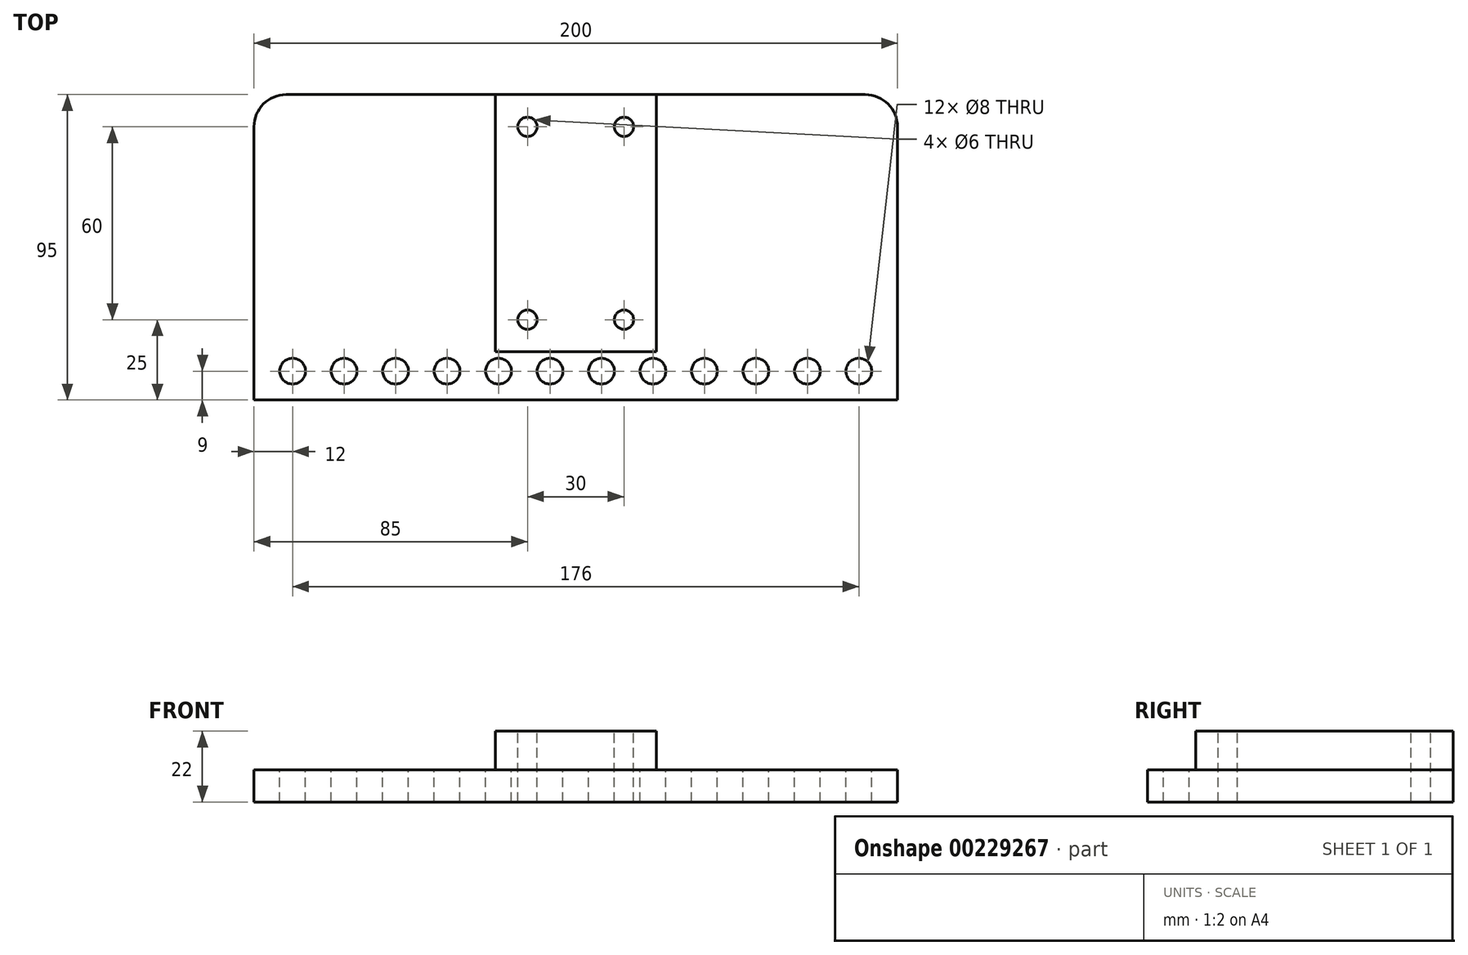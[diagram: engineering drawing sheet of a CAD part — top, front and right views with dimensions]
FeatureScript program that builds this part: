
annotation { "Feature Type Name" : "Feature", "Feature Type Description" : "" }
export const myFeature = defineFeature(function(context is Context, id is Id, definition is map)
    precondition{}
    {
        {
            var Q0;
            Q0=qCreatedBy(makeId("Top.planeOp"),FACE);
            var sketch = newSketch(context, id + "F0", { "sketchPlane" : qUnion([Q0])});
            skLineSegment(sketch, "E0.bottom", {"start": v(0, 0) * mm, "end": v(200, 0) * mm});
            skLineSegment(sketch, "E0.top", {"start": v(10, 95) * mm, "end": v(190, 95) * mm});
            skLineSegment(sketch, "E0.left", {"start": v(0, 0) * mm, "end": v(0, 85) * mm});
            skLineSegment(sketch, "E0.right", {"start": v(200, 0) * mm, "end": v(200, 85) * mm});
            skCircle(sketch, "E1", {"center": v(85, 85) * mm, "radius": 3 * mm});
            skCircle(sketch, "E2.0.1.0", {"center": v(85, 25) * mm, "radius": 3 * mm});
            skCircle(sketch, "E2.1.0.0", {"center": v(115, 85) * mm, "radius": 3 * mm});
            skCircle(sketch, "E2.1.1.0", {"center": v(115, 25) * mm, "radius": 3 * mm});
            skLineSegment(sketch, "E2.direction1", {"start": v(85, 85) * mm, "end": v(115, 85) * mm, "construction": true});
            skLineSegment(sketch, "E2.direction2", {"start": v(85, 85) * mm, "end": v(85, 25) * mm, "construction": true});
            skPoint(sketch, "E3.visualSharp", {"position": v(0, 95) * mm});
            skArc(sketch, "E3.filletArc", {"start": v(10, 95) * mm, "mid": v(2.93, 92.07) * mm, "end": v(0, 85) * mm});
            skPoint(sketch, "E4.visualSharp", {"position": v(200, 95) * mm});
            skArc(sketch, "E4.filletArc", {"start": v(200, 85) * mm, "mid": v(197.07, 92.07) * mm, "end": v(190, 95) * mm});
            skCircle(sketch, "E5", {"center": v(12, 9) * mm, "radius": 4 * mm});
            skCircle(sketch, "E6.1.0.0", {"center": v(28, 9) * mm, "radius": 4 * mm});
            skCircle(sketch, "E6.2.0.0", {"center": v(44, 9) * mm, "radius": 4 * mm});
            skCircle(sketch, "E6.3.0.0", {"center": v(60, 9) * mm, "radius": 4 * mm});
            skLineSegment(sketch, "E6.direction1", {"start": v(12, 9) * mm, "end": v(28, 9) * mm, "construction": true});
            skLineSegment(sketch, "E7", {"start": v(75, 95) * mm, "end": v(75, 15) * mm});
            skLineSegment(sketch, "E8", {"start": v(125, 95) * mm, "end": v(125, 15) * mm});
            skLineSegment(sketch, "E9", {"start": v(75, 15) * mm, "end": v(125, 15) * mm});
            skPoint(sketch, "E10.orphan", {"position": v(125, 0) * mm});
            skPoint(sketch, "E11.orphan", {"position": v(75, 0) * mm});
            skCircle(sketch, "E12.0.4.0", {"center": v(76, 9) * mm, "radius": 4 * mm});
            skCircle(sketch, "E12.0.5.0", {"center": v(92, 9) * mm, "radius": 4 * mm});
            skCircle(sketch, "E13.0.6.0", {"center": v(108, 9) * mm, "radius": 4 * mm});
            skCircle(sketch, "E13.0.7.0", {"center": v(124, 9) * mm, "radius": 4 * mm});
            skCircle(sketch, "E13.0.8.0", {"center": v(140, 9) * mm, "radius": 4 * mm});
            skCircle(sketch, "E14.0.9.0", {"center": v(156, 9) * mm, "radius": 4 * mm});
            skCircle(sketch, "E15.0.10.0", {"center": v(172, 9) * mm, "radius": 4 * mm});
            skCircle(sketch, "E15.0.11.0", {"center": v(188, 9) * mm, "radius": 4 * mm});
            skSolve(sketch);
        }
        {
            var Q0;
            Q0 = qSketchRegion(id + "F0", true);
            extrude(context, id + "F1", {"entities" : qUnion([Q0]), "oppositeDirection" : true, "depth" : 10 * mm});
        }
        {
            var Q0;
            Q0=makeQuery(id+"F0.imprint","IMPRINT",FACE,{"disambiguationData":[TD([[makeQuery(id+"F0.imprint","IMPRINT",EDGE,{"derivedFrom":sQuery(id+"F0.wireOp",EDGE,"E1")}),-1.0]])]});
            extrude(context, id + "F2", {"entities" : qUnion([Q0]), "operationType" : NewBodyOperationType.ADD, "depth" : 12 * mm});
        }
    });
